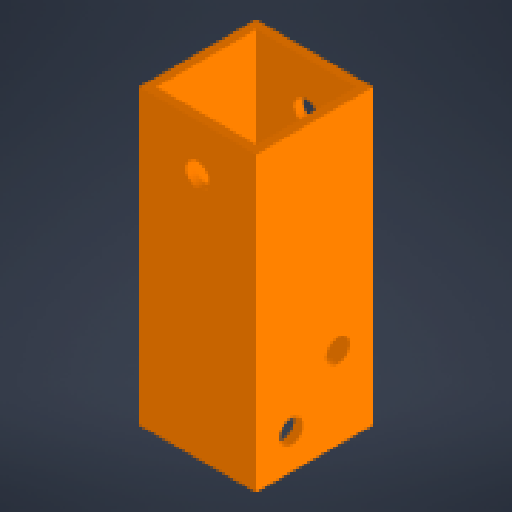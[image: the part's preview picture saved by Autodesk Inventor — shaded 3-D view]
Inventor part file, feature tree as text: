
AUTODESK INVENTOR PART (.ipt)
format: ipt  version: 2024 (Build 280153000, 153)  size: 153,088 bytes
history: native  units: mm
features: reference x5, other x4, extrude x3, sketch x3
ambient origin geometry x8: Origin, YZ Plane, XZ Plane, XY Plane, X Axis, Y Axis, Z Axis, Center Point
bodies: Body1 (feature_tree)
feature tree (15):
  other  "Твердое тело1"
  extrude  "Выдавливание1"  Depth=1.5mm
  extrude  "Выдавливание2"  Depth=50.0mm TaperAngle=0.0deg
  extrude  "Выдавливание3"  TaperAngle=0.0deg  [1 undecoded]
  sketch  "Эскиз1"
  reference  "Ссылка1"
  reference  "Ссылка2"
  sketch  "Эскиз2"
  reference  "Ссылка3"
  reference  "Ссылка4"
  reference  "Ссылка5"
  sketch  "Эскиз3"
  parser-record x1  (decoder bookkeeping rows leaked as tree rows — omitted from the tree; the rows remain in map.json)
  other  "base_assembly.iam"
  other  "square_box_section:1"
note: 1 required parameter value undecoded (feature->parameter linkage not recoverable at this tier; creation-order binding heuristic only, values carry confidence <= 0.55)
note: 1 file-system path scrubbed to <path> (originals preserved in map.json)
